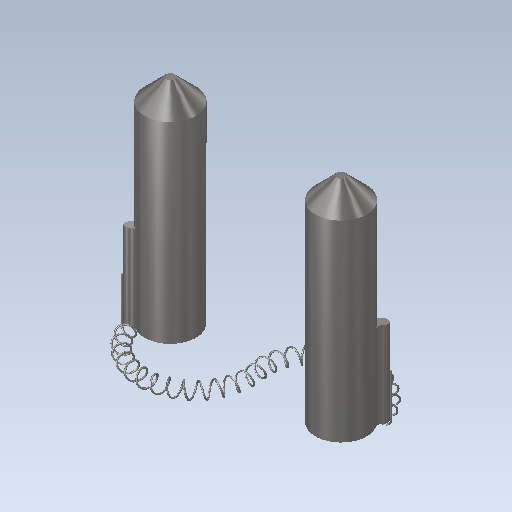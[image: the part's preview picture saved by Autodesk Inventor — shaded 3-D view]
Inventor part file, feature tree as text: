
AUTODESK INVENTOR PART (.ipt)
format: ipt  version: 2020 (Build 240168000, 168)  size: 1,272,832 bytes
history: native  units: in
note: dims shown in document units (in); Inventor stores cm internally (conversion verified against a paired STEP export)
features: projected_geometry x15, sketch x11, extrude x6, sweep x2, chamfer x1, plane x1, other x1
ambient origin geometry x8: Origin, YZ Plane, XZ Plane, XY Plane, X Axis, Y Axis, Z Axis, Center Point
bodies: Solid1 (feature_tree)
feature tree (37):
  extrude  "Extrusion1"  Depth=0.1in
  chamfer  "Chamfer1"  Distance=0.25in
  sketch  "Sketch4"  dims[d2=0.06in d3=0.25in d4=0.0in]
  sweep  "Sweep4"
  extrude  "Extrusion2"  Depth=0.03in
  plane  "Work Plane1"
  extrude  "Extrusion3"  Depth=0.01in
  extrude  "Extrusion4"  Depth=0.0625in
  extrude  "Extrusion5"  TaperAngle=0.0deg  [1 undecoded]
  extrude  "Extrusion6"  Depth=0.05in TaperAngle=0.0deg
  sketch  "Sketch15"  dims[d46=0.012in d47=0.05in d48=0.0in d49=0.05in d50=0.0in d52=45.0deg d53=0.1in d54=0.0in d55=0.1in d56=0.0in]
  sketch  "Sketch1"  dims[d0=0.2in d1=0.1in]
  projected_geometry  "Projected Loop1"
  projected_geometry  "Projected Loop2"
  sketch  "Sketch6"  dims[d5=0.025in d6=0.125in d7=45.0deg d27=45.0deg]
  other  "Srf2"
  sketch  "Sketch9"  dims[d28=0.04in d29=0.03in]
  projected_geometry  "Projected Loop3"
  sketch  "3D Sketch3"
  sketch  "Sketch10"  dims[d30=90.0deg d31=0.01in]
  projected_geometry  "Projected Loop4"
  projected_geometry  "Projected Loop5"
  sketch  "Sketch11"  dims[d32=0.0in d33=68.7138in d37=0.0625in]
  sketch  "Sketch12"  dims[d38=0.002in d39=0.0in d40=0.0in]
  projected_geometry  "Projected Loop6"
  sketch  "Sketch13"  dims[d41=0.019in d42=0.05in d43=0.0in]
  projected_geometry  "Projected Loop7"
  projected_geometry  "Projected Loop8"
  sketch  "Sketch14"  dims[d44=-0.035in d45=0.01in]
  projected_geometry  "Projected Loop9"
  projected_geometry  "Projected Loop10"
  projected_geometry  "Projected Loop11"
  projected_geometry  "Projected Loop12"
  projected_geometry  "Projected Loop13"
  projected_geometry  "Projected Loop14"
  projected_geometry  "Projected Loop15"
  sweep  "SweepSrf2"
note: 1 required parameter value undecoded (feature->parameter linkage not recoverable at this tier; creation-order binding heuristic only, values carry confidence <= 0.55)
